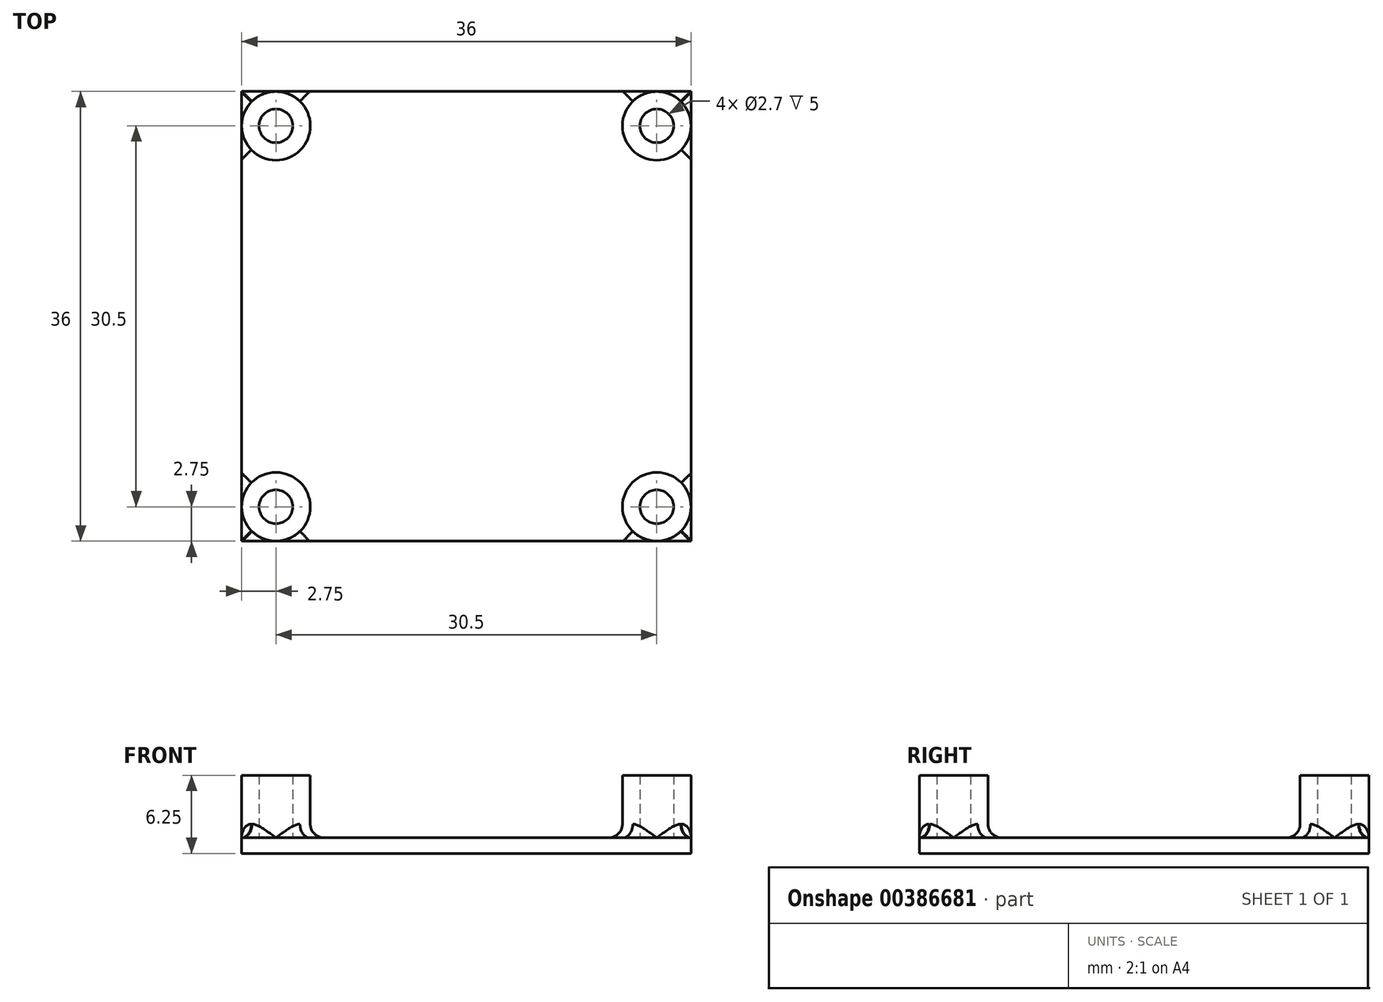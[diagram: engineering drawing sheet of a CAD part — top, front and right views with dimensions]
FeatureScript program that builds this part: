
annotation { "Feature Type Name" : "Feature", "Feature Type Description" : "" }
export const myFeature = defineFeature(function(context is Context, id is Id, definition is map)
    precondition{}
    {
        {
            var Q0;
            Q0=qCreatedBy(makeId("Top.planeOp"),FACE);
            var sketch = newSketch(context, id + "F0", { "sketchPlane" : qUnion([Q0])});
            skLineSegment(sketch, "E0.bottom", {"start": v(0, 0) * mm, "end": v(36, 0) * mm});
            skLineSegment(sketch, "E0.top", {"start": v(0, 36) * mm, "end": v(36, 36) * mm});
            skLineSegment(sketch, "E0.left", {"start": v(0, 0) * mm, "end": v(0, 36) * mm});
            skLineSegment(sketch, "E0.right", {"start": v(36, 0) * mm, "end": v(36, 36) * mm});
            skSolve(sketch);
        }
        {
            var Q0;
            Q0 = qSketchRegion(id + "F0", true);
            extrude(context, id + "F1", {"entities" : qUnion([Q0]), "depth" : 1.25 * mm, "offsetDistance" : 25 * mm});
        }
        {
            var Q0;
            Q0=makeQuery(id+"F1.opExtrude","CAP_FACE",FACE,{"disambiguationData":[OSD([sQuery(id+"F0.wireOp",EDGE,"E0.bottom"),sQuery(id+"F0.wireOp",EDGE,"E0.top"),sQuery(id+"F0.wireOp",EDGE,"E0.left"),sQuery(id+"F0.wireOp",EDGE,"E0.right")])],"isStart":false});
            var sketch = newSketch(context, id + "F2", { "sketchPlane" : qUnion([Q0])});
            skCircle(sketch, "E1", {"center": v(2.75, 2.75) * mm, "radius": 1.35 * mm});
            skCircle(sketch, "E2", {"center": v(33.25, 2.75) * mm, "radius": 1.35 * mm});
            skCircle(sketch, "E3", {"center": v(33.25, 33.25) * mm, "radius": 1.35 * mm});
            skCircle(sketch, "E4", {"center": v(2.75, 33.25) * mm, "radius": 1.35 * mm});
            skCircle(sketch, "E5", {"center": v(2.75, 33.25) * mm, "radius": 2.75 * mm});
            skCircle(sketch, "E6", {"center": v(33.25, 33.25) * mm, "radius": 2.75 * mm});
            skCircle(sketch, "E7", {"center": v(33.25, 2.75) * mm, "radius": 2.75 * mm});
            skCircle(sketch, "E8", {"center": v(2.75, 2.75) * mm, "radius": 2.75 * mm});
            skSolve(sketch);
        }
        {
            var Q0;
            Q0 = qSketchRegion(id + "F2", true);
            extrude(context, id + "F3", {"entities" : qUnion([Q0]), "operationType" : NewBodyOperationType.ADD, "depth" : 5 * mm, "offsetDistance" : 25 * mm});
        }
        {
            var Q0;
            Q0=makeQuery(id+"F3.boolean.opBoolean","SPLIT",EDGE,{"disambiguationData":[OD(1.0)],"derivedFrom":makeQuery(id+"F3.opExtrude","CAP_EDGE",EDGE,{"disambiguationData":[OSD([sQuery(id+"F2.wireOp",EDGE,"E5")])],"isStart":true})});
            var Q1;
            Q1=makeQuery(id+"F3.boolean.opBoolean","SPLIT",EDGE,{"disambiguationData":[OD(1.0)],"derivedFrom":makeQuery(id+"F3.opExtrude","CAP_EDGE",EDGE,{"disambiguationData":[OSD([sQuery(id+"F2.wireOp",EDGE,"E6")])],"isStart":true})});
            var Q2;
            Q2=makeQuery(id+"F3.boolean.opBoolean","SPLIT",EDGE,{"disambiguationData":[OD(1.0)],"derivedFrom":makeQuery(id+"F3.opExtrude","CAP_EDGE",EDGE,{"disambiguationData":[OSD([sQuery(id+"F2.wireOp",EDGE,"E7")])],"isStart":true})});
            var Q3;
            Q3=makeQuery(id+"F3.boolean.opBoolean","SPLIT",EDGE,{"disambiguationData":[OD(1.0)],"derivedFrom":makeQuery(id+"F3.opExtrude","CAP_EDGE",EDGE,{"disambiguationData":[OSD([sQuery(id+"F2.wireOp",EDGE,"E8")])],"isStart":true})});
            fillet(context, id + "F4", {"entities" : qUnion([Q0, Q1, Q2, Q3]), "radius" : 1.1 * mm, "tangentPropagation" : true, "allowEdgeOverflow" : false});
        }
    });
